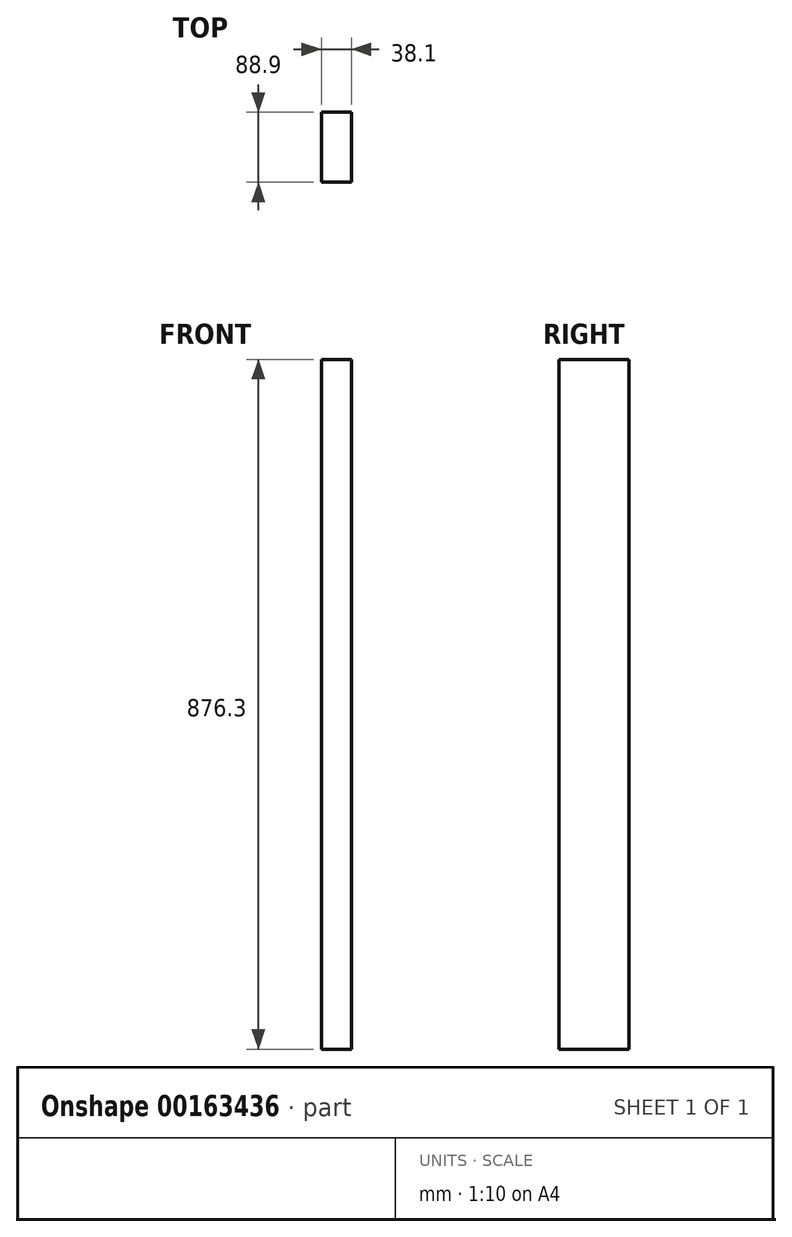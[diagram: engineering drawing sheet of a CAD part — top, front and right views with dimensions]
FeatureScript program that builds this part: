
annotation { "Feature Type Name" : "Feature", "Feature Type Description" : "" }
export const myFeature = defineFeature(function(context is Context, id is Id, definition is map)
    precondition{}
    {
        {
            var Q0;
            Q0=qCreatedBy(makeId("Top.planeOp"),FACE);
            var sketch = newSketch(context, id + "F0", { "sketchPlane" : qUnion([Q0])});
            skLineSegment(sketch, "E0.bottom", {"start": v(0, 0) * mm, "end": v(38.1, 0) * mm});
            skLineSegment(sketch, "E0.top", {"start": v(0, 88.9) * mm, "end": v(38.1, 88.9) * mm});
            skLineSegment(sketch, "E0.left", {"start": v(0, 0) * mm, "end": v(0, 88.9) * mm});
            skLineSegment(sketch, "E0.right", {"start": v(38.1, 0) * mm, "end": v(38.1, 88.9) * mm});
            skSolve(sketch);
        }
        {
            var Q0;
            Q0 = qSketchRegion(id + "F0", true);
            extrude(context, id + "F1", {"entities" : qUnion([Q0]), "depth" : 876.3 * mm});
        }
    });
